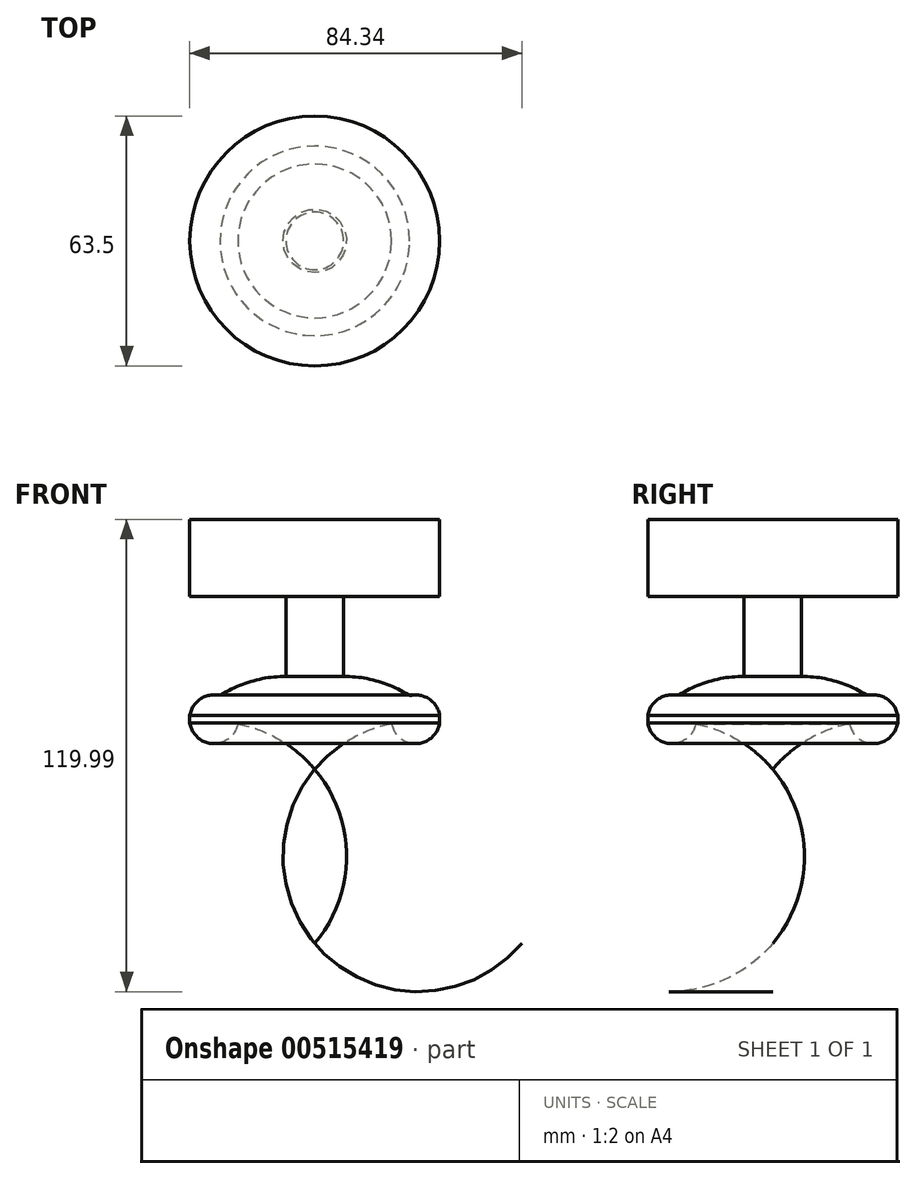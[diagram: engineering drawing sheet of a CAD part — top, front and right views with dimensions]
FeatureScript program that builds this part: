
annotation { "Feature Type Name" : "Feature", "Feature Type Description" : "" }
export const myFeature = defineFeature(function(context is Context, id is Id, definition is map)
    precondition{}
    {
        {
            var Q0;
            Q0=qCreatedBy(makeId("Front.planeOp"),FACE);
            var sketch = newSketch(context, id + "F0", { "sketchPlane" : qUnion([Q0])});
            skLineSegment(sketch, "E0", {"start": v(31.75, 11.8) * mm, "end": v(31.75, 13.64) * mm});
            skLineSegment(sketch, "E1", {"start": v(7.33, 23.6) * mm, "end": v(7.33, 43.96) * mm});
            skLineSegment(sketch, "E2", {"start": v(7.33, 43.96) * mm, "end": v(31.75, 43.96) * mm});
            skLineSegment(sketch, "E3", {"start": v(31.75, 43.96) * mm, "end": v(31.75, 63.5) * mm});
            skLineSegment(sketch, "E4", {"start": v(31.75, 63.5) * mm, "end": v(0, 63.5) * mm});
            skLineSegment(sketch, "E5", {"start": v(0, 63.5) * mm, "end": v(0, 0) * mm});
            skArc(sketch, "E6", {"start": v(31.75, 11.8) * mm, "mid": v(14.32, 10.09) * mm, "end": v(0, 0) * mm});
            skArc(sketch, "E7", {"start": v(31.75, 11.8) * mm, "mid": v(20.9, 20.5) * mm, "end": v(7.33, 23.6) * mm});
            skArc(sketch, "E8", {"start": v(19.54, 11.57) * mm, "mid": v(30.85, 9.4) * mm, "end": v(24.08, 18.72) * mm});
            skPoint(sketch, "E8.startSnap0", {"position": v(19.54, 23.6) * mm});
            skPoint(sketch, "E9.orphan", {"position": v(31.75, 23.6) * mm});
            skPoint(sketch, "E10.end.orphan", {"position": v(31.75, 0) * mm});
            skSolve(sketch);
        }
        {
            var Q0;
            {var subQ0=sQuery(id+"F0.wireOp",EDGE,"E1");Q0=makeQuery(id+"F0.imprint","IMPRINT",FACE,{"disambiguationData":[TD([[makeQuery(id+"F0.imprint","IMPRINT",EDGE,{"derivedFrom":subQ0}),1.0]])]});}
            var Q1;
            {var subQ0=sQuery(id+"F0.wireOp",EDGE,"E8");var subQ1=sQuery(id+"F0.wireOp",EDGE,"E6");var subQ3=makeQuery(id+"F0.imprint","INTERSECT",VERTEX,{"derivedFrom":[subQ1,subQ0]});Q1=makeQuery(id+"F0.imprint","IMPRINT",FACE,{"disambiguationData":[TD([[makeQuery(id+"F0.imprint","IMPRINT",EDGE,{"disambiguationData":[TD([[subQ3,1.0]])],"derivedFrom":subQ1}),1.0]])]});}
            var Q2;
            {var subQ0=sQuery(id+"F0.wireOp",EDGE,"E0");Q2=makeQuery(id+"F0.imprint","IMPRINT",FACE,{"disambiguationData":[TD([[makeQuery(id+"F0.imprint","IMPRINT",EDGE,{"derivedFrom":subQ0}),1.0]])]});}
            var Q3;
            Q3=sQuery(id+"F0.wireOp",EDGE,"E5");
            revolve(context, id + "F1", {"entities" : qUnion([Q0, Q1, Q2]), "axis" : qUnion([Q3]), "revolveType" : RevolveType.FULL});
        }
    });
